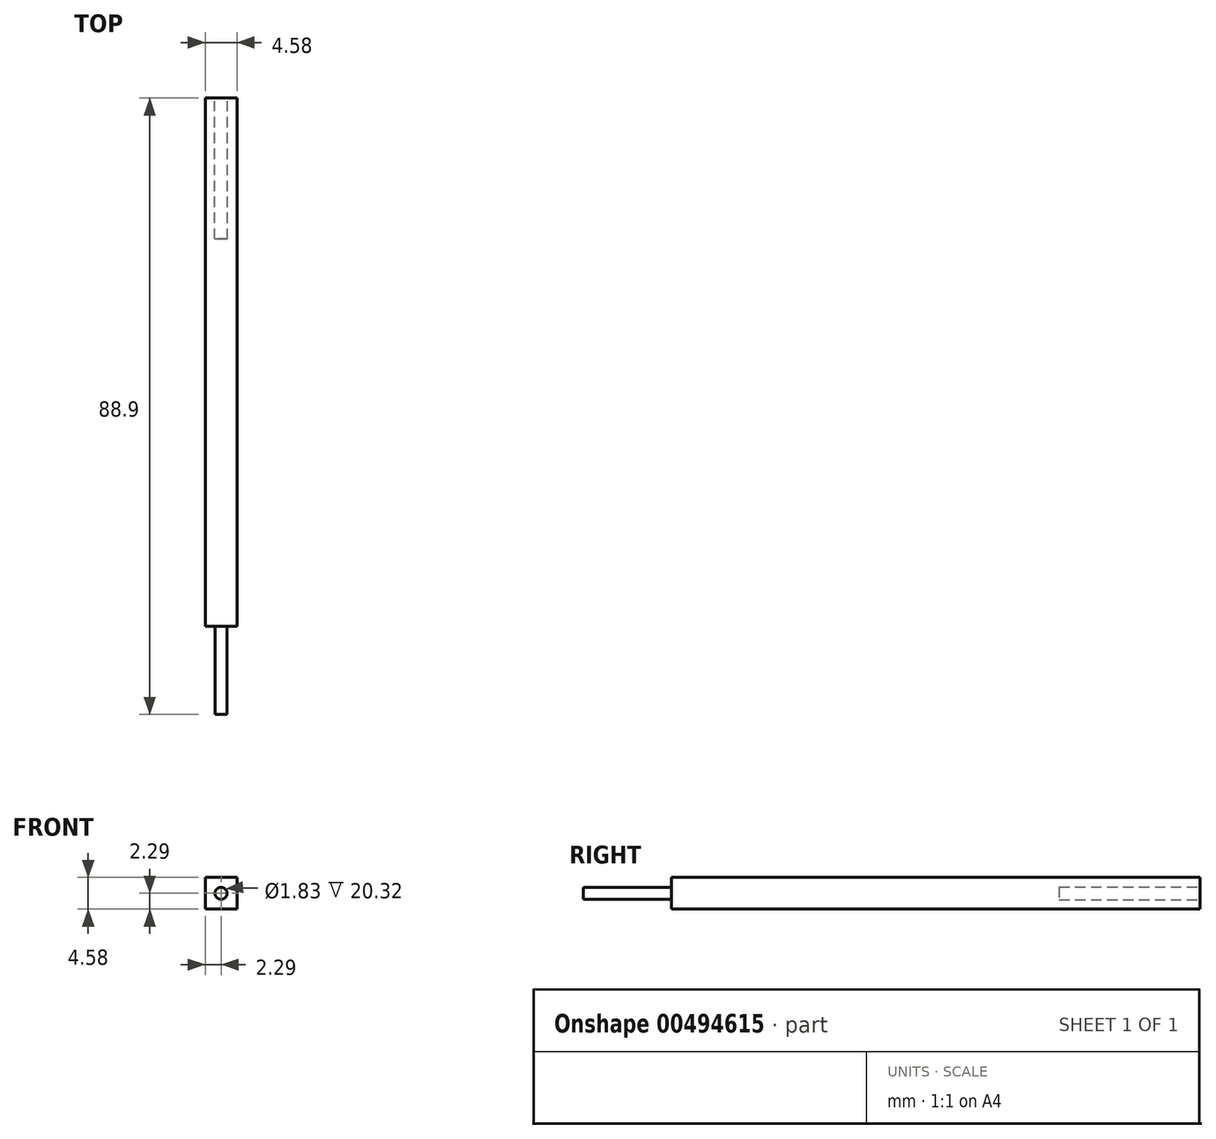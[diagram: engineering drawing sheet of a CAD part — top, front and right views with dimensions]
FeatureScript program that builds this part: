
annotation { "Feature Type Name" : "Feature", "Feature Type Description" : "" }
export const myFeature = defineFeature(function(context is Context, id is Id, definition is map)
    precondition{}
    {
        {
            var Q0;
            Q0=qCreatedBy(makeId("Front.planeOp"),FACE);
            var sketch = newSketch(context, id + "F0", { "sketchPlane" : qUnion([Q0])});
            skLineSegment(sketch, "E0.bottom", {"start": v(-2.29, 2.29) * mm, "end": v(2.29, 2.29) * mm});
            skLineSegment(sketch, "E0.top", {"start": v(-2.29, -2.29) * mm, "end": v(2.29, -2.29) * mm});
            skLineSegment(sketch, "E0.left", {"start": v(-2.29, 2.29) * mm, "end": v(-2.29, -2.29) * mm});
            skLineSegment(sketch, "E0.right", {"start": v(2.29, 2.29) * mm, "end": v(2.29, -2.29) * mm});
            skSolve(sketch);
        }
        {
            var Q0;
            Q0=makeQuery(id+"F0.imprint","IMPRINT",FACE,{"disambiguationData":[TD([[makeQuery(id+"F0.imprint","IMPRINT",EDGE,{"derivedFrom":sQuery(id+"F0.wireOp",EDGE,"E0.bottom")}),-1.0]])]});
            extrude(context, id + "F1", {"entities" : qUnion([Q0]), "depth" : 76.2 * mm});
        }
        {
            var Q0;
            Q0=makeQuery(id+"F1.opExtrude","CAP_FACE",FACE,{"disambiguationData":[OSD([sQuery(id+"F0.wireOp",EDGE,"E0.bottom"),sQuery(id+"F0.wireOp",EDGE,"E0.top"),sQuery(id+"F0.wireOp",EDGE,"E0.left"),sQuery(id+"F0.wireOp",EDGE,"E0.right")])],"isStart":false});
            var sketch = newSketch(context, id + "F2", { "sketchPlane" : qUnion([Q0])});
            skCircle(sketch, "E1", {"center": v(0, 0) * mm, "radius": 0.88 * mm});
            skSolve(sketch);
        }
        {
            var Q0;
            Q0=makeQuery(id+"F2.imprint","IMPRINT",FACE,{"disambiguationData":[TD([[makeQuery(id+"F2.imprint","IMPRINT",EDGE,{"derivedFrom":sQuery(id+"F2.wireOp",EDGE,"E1")}),1.0]])]});
            extrude(context, id + "F3", {"entities" : qUnion([Q0]), "operationType" : NewBodyOperationType.ADD, "depth" : 12.7 * mm});
        }
        {
            var Q0;
            Q0=makeQuery(id+"F1.opExtrude","CAP_FACE",FACE,{"disambiguationData":[OSD([sQuery(id+"F0.wireOp",EDGE,"E0.bottom"),sQuery(id+"F0.wireOp",EDGE,"E0.top"),sQuery(id+"F0.wireOp",EDGE,"E0.left"),sQuery(id+"F0.wireOp",EDGE,"E0.right")])],"isStart":true});
            var sketch = newSketch(context, id + "F4", { "sketchPlane" : qUnion([Q0])});
            skCircle(sketch, "E2", {"center": v(0, 0) * mm, "radius": 0.91 * mm});
            skSolve(sketch);
        }
        {
            var Q0;
            Q0=makeQuery(id+"F4.imprint","IMPRINT",FACE,{"disambiguationData":[TD([[makeQuery(id+"F4.imprint","IMPRINT",EDGE,{"derivedFrom":sQuery(id+"F4.wireOp",EDGE,"E2")}),1.0]])]});
            extrude(context, id + "F5", {"entities" : qUnion([Q0]), "operationType" : NewBodyOperationType.REMOVE, "oppositeDirection" : true, "depth" : 20.32 * mm});
        }
    });
